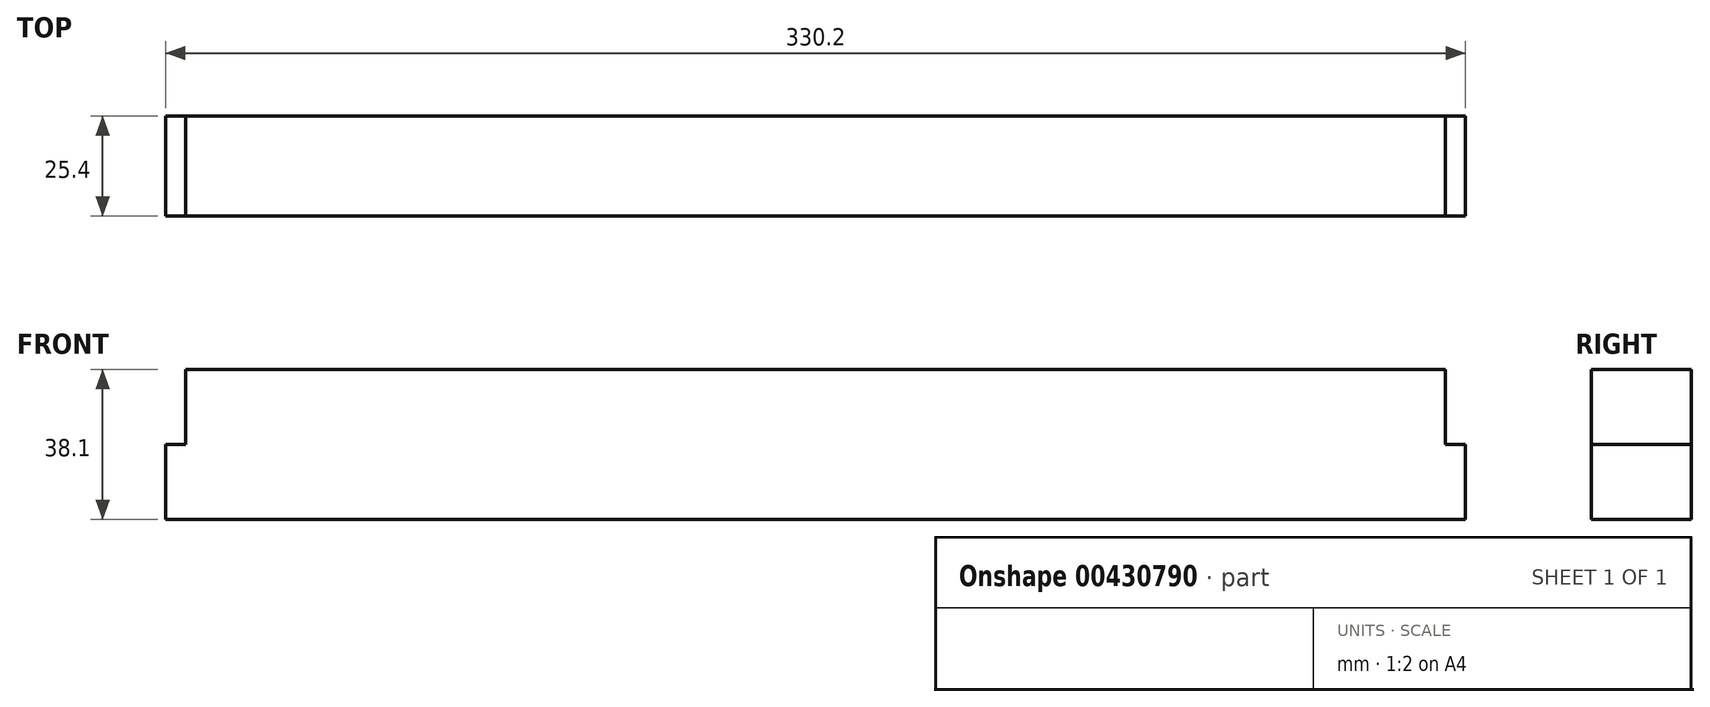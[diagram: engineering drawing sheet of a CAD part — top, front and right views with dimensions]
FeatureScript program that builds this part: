
annotation { "Feature Type Name" : "Feature", "Feature Type Description" : "" }
export const myFeature = defineFeature(function(context is Context, id is Id, definition is map)
    precondition{}
    {
        {
            var Q0;
            Q0=qCreatedBy(makeId("Front.planeOp"),FACE);
            var sketch = newSketch(context, id + "F0", { "sketchPlane" : qUnion([Q0])});
            skLineSegment(sketch, "E0.bottom", {"start": v(0, 0) * mm, "end": v(330.2, 0) * mm});
            skLineSegment(sketch, "E0.top", {"start": v(5.08, 38.1) * mm, "end": v(325.12, 38.1) * mm});
            skLineSegment(sketch, "E0.left", {"start": v(0, 0) * mm, "end": v(0, 19.05) * mm});
            skLineSegment(sketch, "E0.right", {"start": v(330.2, 0) * mm, "end": v(330.2, 19.05) * mm});
            skLineSegment(sketch, "E1.top", {"start": v(0, 19.05) * mm, "end": v(5.08, 19.05) * mm});
            skLineSegment(sketch, "E1.right", {"start": v(5.08, 38.1) * mm, "end": v(5.08, 19.05) * mm});
            skLineSegment(sketch, "E2.top", {"start": v(330.2, 19.05) * mm, "end": v(325.12, 19.05) * mm});
            skLineSegment(sketch, "E2.right", {"start": v(325.12, 38.1) * mm, "end": v(325.12, 19.05) * mm});
            skSolve(sketch);
        }
        {
            var Q0;
            Q0 = qSketchRegion(id + "F0", true);
            extrude(context, id + "F1", {"entities" : qUnion([Q0]), "depth" : 25.4 * mm});
        }
    });
